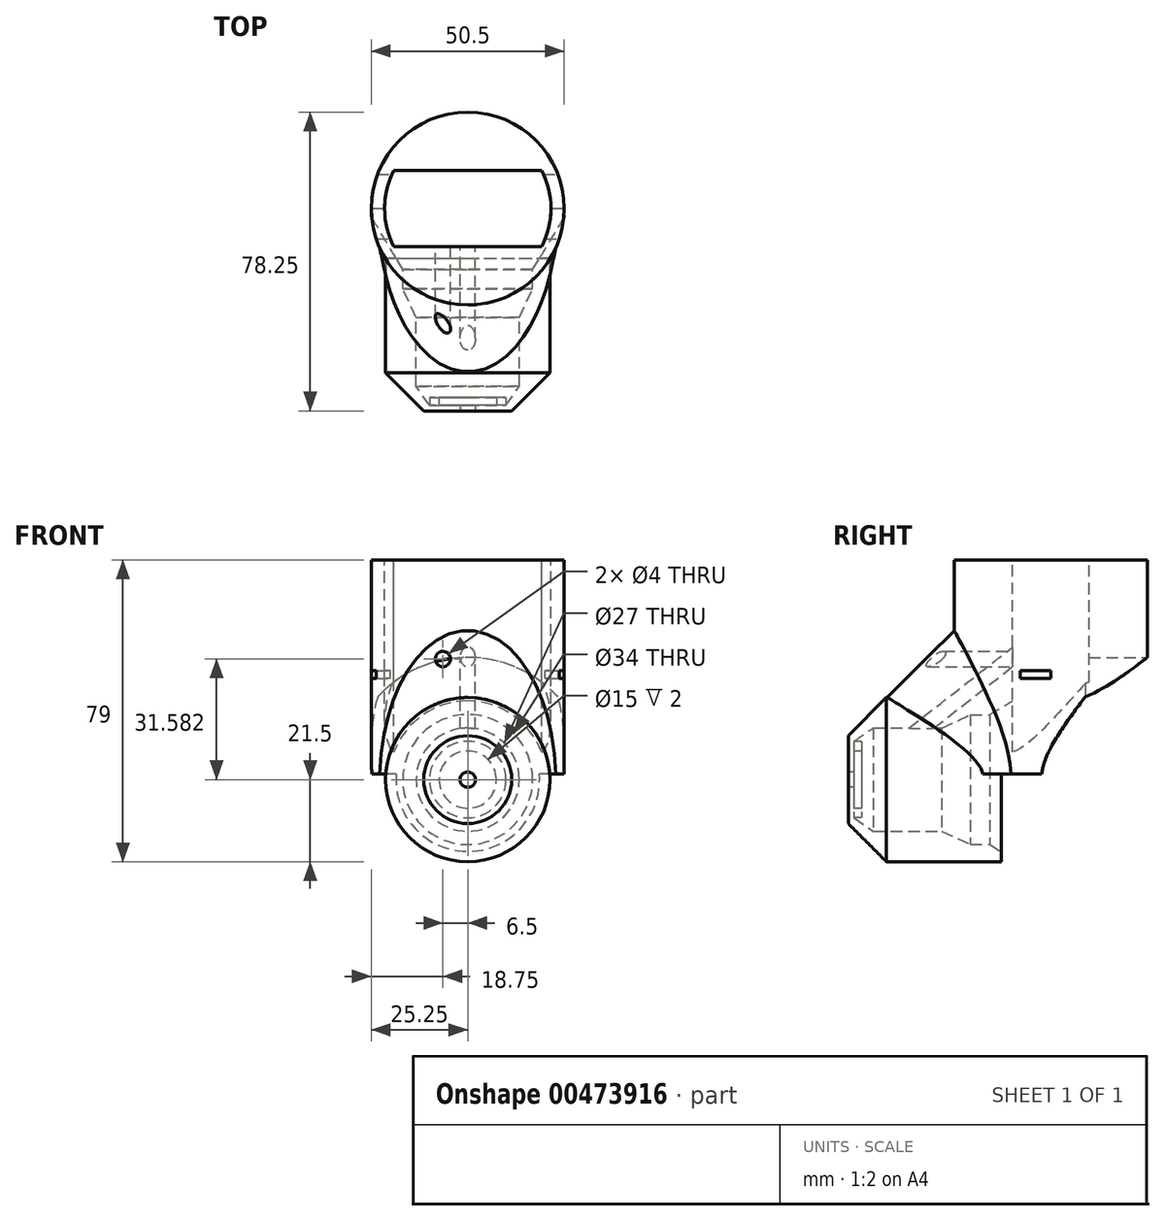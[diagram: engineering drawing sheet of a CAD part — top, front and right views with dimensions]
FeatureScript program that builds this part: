
annotation { "Feature Type Name" : "Feature", "Feature Type Description" : "" }
export const myFeature = defineFeature(function(context is Context, id is Id, definition is map)
    precondition{}
    {
        {
            var Q0;
            Q0=qCreatedBy(makeId("Front.planeOp"),FACE);
            cPlane(context, id + "F0", {"entities" : qUnion([Q0]), "cplaneType" : CPlaneType.OFFSET, "offset" : 10 * mm, "width" : 150 * mm, "height" : 150 * mm});
        }
        {
            var Q0;
            Q0=qCreatedBy(id+"F0.planeOp",FACE);
            var sketch = newSketch(context, id + "F1", { "sketchPlane" : qUnion([Q0])});
            skCircle(sketch, "E0", {"center": v(0, 0) * mm, "radius": 21.5 * mm});
            skSolve(sketch);
        }
        {
            var Q0;
            Q0 = qSketchRegion(id + "F1", true);
            var Q1;
            Q1=makeQuery(id+"F7.opRevolve","SWEPT_BODY",BODY,{"disambiguationData":[OSD([sQuery(id+"F3.wireOp",EDGE,"6SwW3zrQ-XrUX-YoM6-tKD7-60mYdjqLGmun"),sQuery(id+"F3.wireOp",EDGE,"E1"),sQuery(id+"F3.wireOp",EDGE,"E2"),sQuery(id+"F3.wireOp",EDGE,"E3"),sQuery(id+"F3.wireOp",EDGE,"E4"),sQuery(id+"F3.wireOp",EDGE,"E5"),sQuery(id+"F3.wireOp",EDGE,"E6"),sQuery(id+"F3.wireOp",EDGE,"E7")])]});
            extrude(context, id + "F2", {"entities" : qUnion([Q0]), "oppositeDirection" : true, "endBoundEntityBody" : qUnion([Q1]), "depth" : 40 * mm});
        }
        {
            var Q0;
            Q0=qCreatedBy(makeId("Top.planeOp"),FACE);
            var sketch = newSketch(context, id + "F3", { "sketchPlane" : qUnion([Q0])});
            skLineSegment(sketch, "E1", {"start": v(13.5, -3.5) * mm, "end": v(13.5, 14.5) * mm});
            skLineSegment(sketch, "E2", {"start": v(13.5, 14.5) * mm, "end": v(17, 22) * mm});
            skLineSegment(sketch, "E3", {"start": v(17, 22) * mm, "end": v(17, 27) * mm});
            skLineSegment(sketch, "E4", {"start": v(17, 27) * mm, "end": v(32, 52) * mm});
            skLineSegment(sketch, "E5", {"start": v(32, 52) * mm, "end": v(32, 83) * mm});
            skLineSegment(sketch, "E6", {"start": v(32, 83) * mm, "end": v(0, 83) * mm});
            skLineSegment(sketch, "E7", {"start": v(0, 83) * mm, "end": v(0, 0) * mm});
            skLineSegment(sketch, "E8", {"start": v(0, 0) * mm, "end": v(0, -8.5) * mm});
            skLineSegment(sketch, "E9", {"start": v(0, -8.5) * mm, "end": v(10, -8.5) * mm});
            skLineSegment(sketch, "E10", {"start": v(10, -8.5) * mm, "end": v(13.5, -3.5) * mm});
            skSolve(sketch);
        }
        {
            var Q0;
            Q0=qCreatedBy(makeId("Top.planeOp"),FACE);
            cPlane(context, id + "F4", {"entities" : qUnion([Q0]), "cplaneType" : CPlaneType.OFFSET, "offset" : 57.5 * mm, "width" : 150 * mm, "height" : 150 * mm});
        }
        {
            var Q0;
            Q0=qCreatedBy(id+"F4.planeOp",FACE);
            var sketch = newSketch(context, id + "F5", { "sketchPlane" : qUnion([Q0])});
            skArc(sketch, "E11", {"start": v(-19.31, 53) * mm, "mid": v(-21.75, 43) * mm, "end": v(-19.31, 33) * mm});
            skLineSegment(sketch, "E12", {"start": v(-19.31, 53) * mm, "end": v(19.31, 53) * mm});
            skLineSegment(sketch, "E13", {"start": v(-19.31, 33) * mm, "end": v(19.31, 33) * mm});
            skCircle(sketch, "E14", {"center": v(0, 43) * mm, "radius": 25.25 * mm});
            skArc(sketch, "E15.trimOffspring", {"start": v(19.31, 33) * mm, "mid": v(21.75, 43) * mm, "end": v(19.31, 53) * mm});
            skSolve(sketch);
        }
        {
            var Q0;
            Q0 = qSketchRegion(id + "F5", true);
            extrude(context, id + "F6", {"entities" : qUnion([Q0]), "operationType" : NewBodyOperationType.ADD, "oppositeDirection" : true, "depth" : 56 * mm});
        }
        {
            var Q0;
            Q0 = qSketchRegion(id + "F3", true);
            var Q1;
            Q1=sQuery(id+"F3.wireOp",EDGE,"E7");
            revolve(context, id + "F7", {"operationType" : NewBodyOperationType.REMOVE, "entities" : qUnion([Q0]), "axis" : qUnion([Q1]), "revolveType" : RevolveType.FULL});
        }
        {
            var Q0;
            Q0=qCreatedBy(makeId("Top.planeOp"),FACE);
            var Q1;
            Q1=makeQuery(id+"F6.opExtrude","CAP_EDGE",EDGE,{"disambiguationData":[OSD([sQuery(id+"F5.wireOp",EDGE,"E13")])],"isStart":true});
            cPlane(context, id + "F8", {"entities" : qUnion([Q0, Q1]), "cplaneType" : CPlaneType.LINE_ANGLE, "offset" : 25 * mm, "angle" : 128 * degree, "width" : 150 * mm, "height" : 150 * mm});
        }
        {
            var Q0;
            Q0=qCreatedBy(id+"F8.planeOp",FACE);
            var sketch = newSketch(context, id + "F9", { "sketchPlane" : qUnion([Q0])});
            skCircle(sketch, "E16", {"center": v(0, 5) * mm, "radius": 2 * mm});
            skSolve(sketch);
        }
        {
            var Q0;
            Q0 = qSketchRegion(id + "F9", true);
            extrude(context, id + "F10", {"entities" : qUnion([Q0]), "operationType" : NewBodyOperationType.REMOVE, "oppositeDirection" : true, "depth" : 58.9 * mm});
        }
        {
            var Q0;
            Q0=makeQuery(id+"F7.boolean.opBoolean","COPY",FACE,{"derivedFrom":makeQuery(id+"F7.opRevolve","SWEPT_FACE",FACE,{"disambiguationData":[OSD([sQuery(id+"F3.wireOp",EDGE,"E9")])]})});
            var sketch = newSketch(context, id + "F11", { "sketchPlane" : qUnion([Q0])});
            skCircle(sketch, "E17", {"center": v(0, 0) * mm, "radius": 7.5 * mm});
            skCircle(sketch, "E18", {"center": v(0, 0) * mm, "radius": 10 * mm});
            skSolve(sketch);
        }
        {
            var Q0;
            Q0 = qSketchRegion(id + "F11", true);
            extrude(context, id + "F12", {"entities" : qUnion([Q0]), "operationType" : NewBodyOperationType.ADD, "depth" : 2 * mm});
        }
        {
            var Q0;
            Q0=makeQuery(id+"F6.opExtrude","SWEPT_FACE",FACE,{"disambiguationData":[OSD([sQuery(id+"F5.wireOp",EDGE,"E13")])]});
            var sketch = newSketch(context, id + "F13", { "sketchPlane" : qUnion([Q0])});
            skCircle(sketch, "E19", {"center": v(6.5, 31.58) * mm, "radius": 2 * mm});
            skSolve(sketch);
        }
        {
            var Q0;
            Q0 = qSketchRegion(id + "F13", true);
            extrude(context, id + "F14", {"entities" : qUnion([Q0]), "operationType" : NewBodyOperationType.REMOVE, "oppositeDirection" : true, "depth" : 25 * mm});
        }
        {
            var Q0;
            Q0=makeQuery(id+"F2.opExtrude","CAP_FACE",FACE,{"disambiguationData":[OSD([sQuery(id+"F1.wireOp",EDGE,"E0")])],"isStart":true});
            var sketch = newSketch(context, id + "F15", { "sketchPlane" : qUnion([Q0])});
            skCircle(sketch, "E20", {"center": v(0, 0) * mm, "radius": 2 * mm});
            skSolve(sketch);
        }
        {
            var Q0;
            Q0 = qSketchRegion(id + "F15", true);
            extrude(context, id + "F16", {"entities" : qUnion([Q0]), "operationType" : NewBodyOperationType.REMOVE, "oppositeDirection" : true, "depth" : 25 * mm});
        }
        {
            var Q0;
            Q0=qCreatedBy(makeId("Right.planeOp"),FACE);
            var sketch = newSketch(context, id + "F17", { "sketchPlane" : qUnion([Q0])});
            skLineSegment(sketch, "E21.bottom", {"start": v(35, 26.5) * mm, "end": v(43, 26.5) * mm});
            skLineSegment(sketch, "E21.top", {"start": v(35, 28.5) * mm, "end": v(43, 28.5) * mm});
            skLineSegment(sketch, "E21.left", {"start": v(35, 26.5) * mm, "end": v(35, 28.5) * mm});
            skLineSegment(sketch, "E21.right", {"start": v(43, 26.5) * mm, "end": v(43, 28.5) * mm});
            skSolve(sketch);
        }
        {
            var Q0;
            Q0 = qSketchRegion(id + "F17", true);
            extrude(context, id + "F18", {"entities" : qUnion([Q0]), "operationType" : NewBodyOperationType.REMOVE, "endBound" : BoundingType.SYMMETRIC, "oppositeDirection" : true, "depth" : 69.8 * mm});
        }
        {
            var Q0;
            Q0=makeQuery(id+"F2.opExtrude","CAP_EDGE",EDGE,{"disambiguationData":[OSD([sQuery(id+"F1.wireOp",EDGE,"E0")])],"isStart":true});
            chamfer(context, id + "F19", {"entities" : qUnion([Q0]), "width" : 10 * mm, "tangentPropagation" : true});
        }
        {
            var Q0;
            Q0=makeQuery(id+"F10.boolean.opBoolean","SPLIT",EDGE,{"disambiguationData":[OD(1.0)],"derivedFrom":makeQuery(id+"F6.boolean.opBoolean","INTERSECT",EDGE,{"derivedFrom":[makeQuery(id+"F2.opExtrude","SWEPT_FACE",FACE,{"disambiguationData":[OSD([sQuery(id+"F1.wireOp",EDGE,"E0")])]}),makeQuery(id+"F6.opExtrude","SWEPT_FACE",FACE,{"disambiguationData":[OSD([sQuery(id+"F5.wireOp",EDGE,"E14")])]})]})});
            chamfer(context, id + "F20", {"entities" : qUnion([Q0]), "width" : 17.5 * mm, "tangentPropagation" : true});
        }
    });
